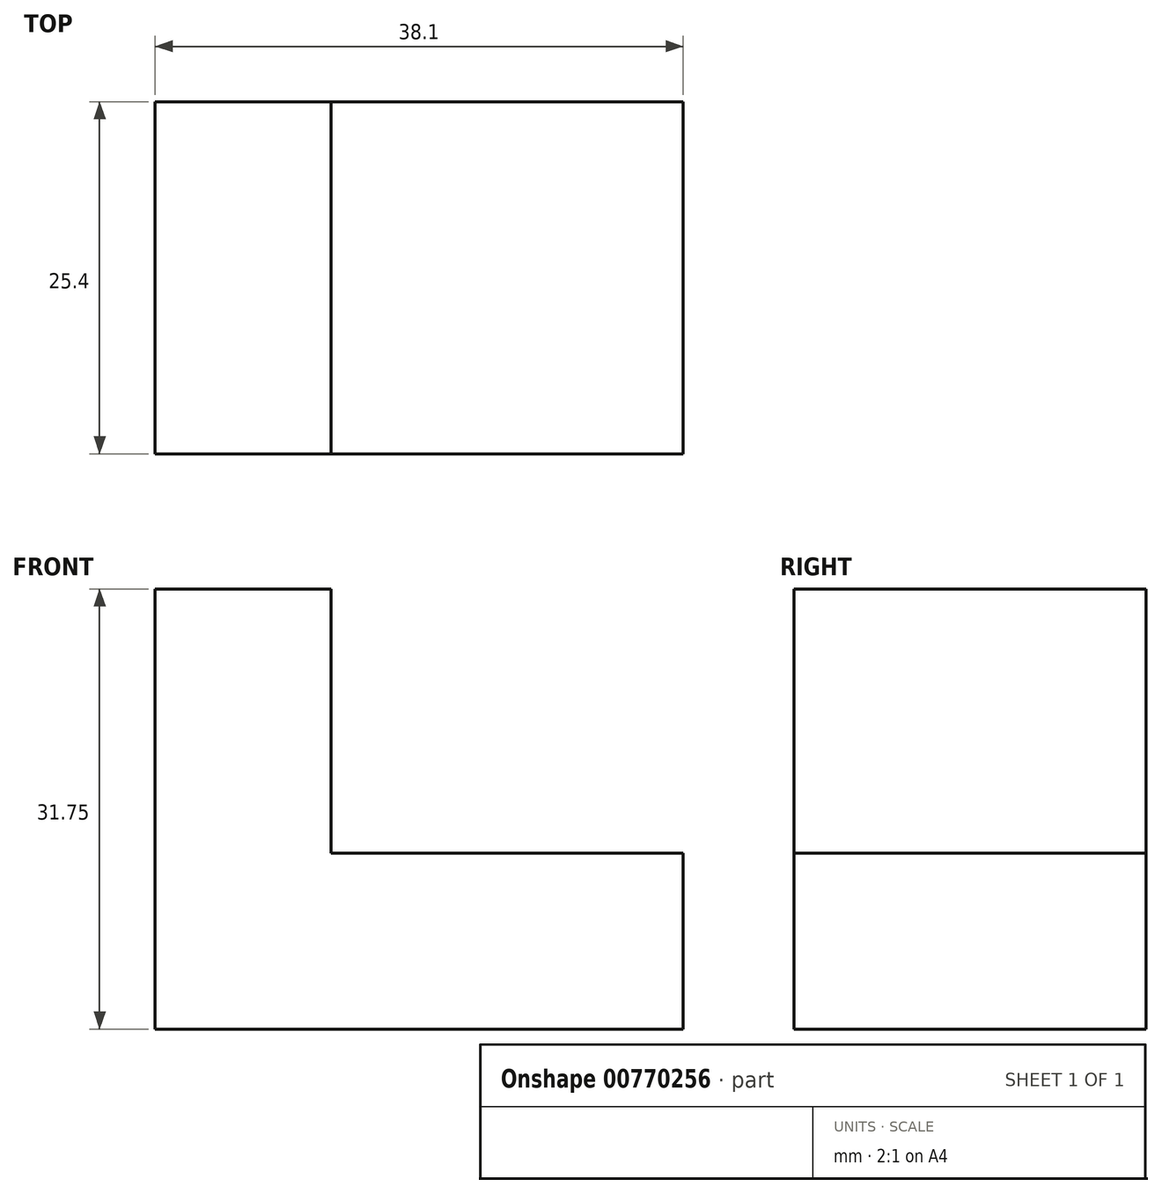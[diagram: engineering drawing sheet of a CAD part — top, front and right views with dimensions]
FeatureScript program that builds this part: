
annotation { "Feature Type Name" : "Feature", "Feature Type Description" : "" }
export const myFeature = defineFeature(function(context is Context, id is Id, definition is map)
    precondition{}
    {
        {
            var Q0;
            Q0=qCreatedBy(makeId("Front.planeOp"),FACE);
            var sketch = newSketch(context, id + "F0", { "sketchPlane" : qUnion([Q0])});
            skLineSegment(sketch, "E0", {"start": v(0, 0) * mm, "end": v(25.4, 0) * mm});
            skLineSegment(sketch, "E1", {"start": v(25.4, -12.7) * mm, "end": v(25.4, 0) * mm});
            skLineSegment(sketch, "E2", {"start": v(25.4, -12.7) * mm, "end": v(-12.7, -12.7) * mm});
            skLineSegment(sketch, "E3", {"start": v(-12.7, 19.05) * mm, "end": v(-12.7, -12.7) * mm});
            skLineSegment(sketch, "E4", {"start": v(-12.7, 19.05) * mm, "end": v(0, 19.05) * mm});
            skLineSegment(sketch, "E5", {"start": v(0, 19.05) * mm, "end": v(0, 0) * mm});
            skSolve(sketch);
        }
        {
            var Q0;
            Q0=makeQuery(id+"F0.imprint","IMPRINT",FACE,{"disambiguationData":[TD([[makeQuery(id+"F0.imprint","IMPRINT",EDGE,{"derivedFrom":sQuery(id+"F0.wireOp",EDGE,"E0")}),-1.0]])]});
            extrude(context, id + "F1", {"entities" : qUnion([Q0]), "depth" : 25.4 * mm, "offsetDistance" : 25.4 * mm});
        }
    });
